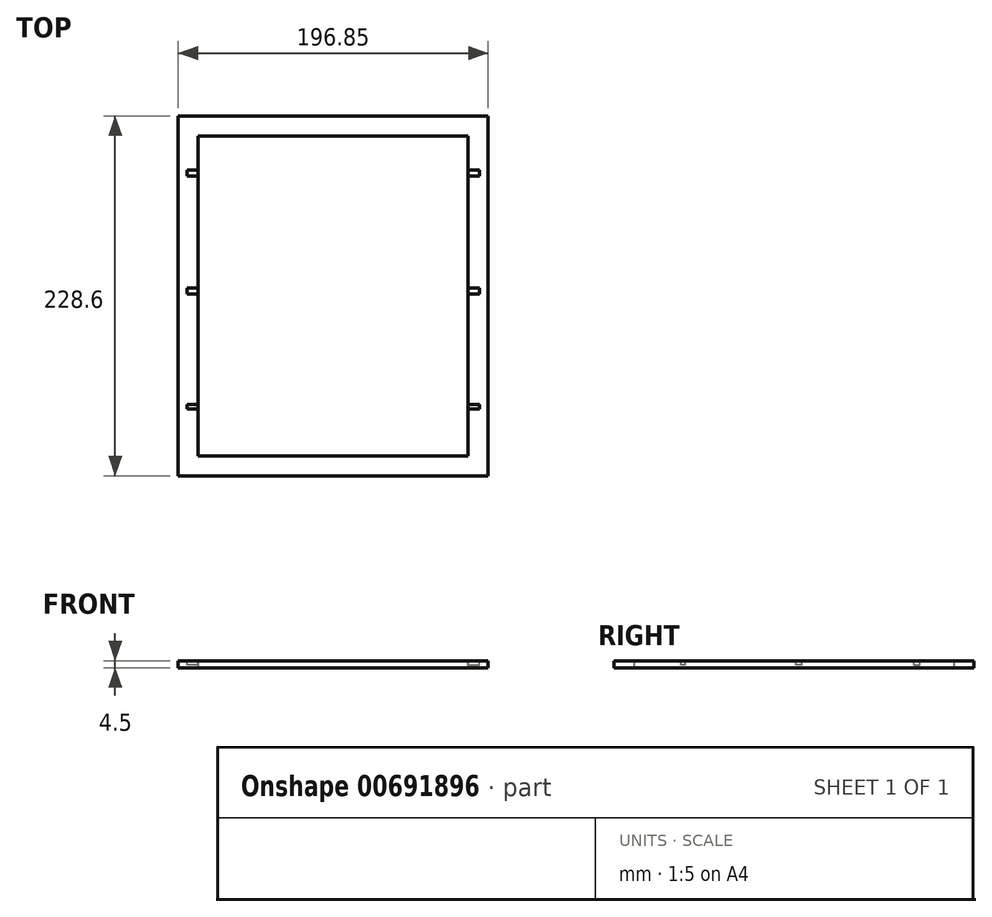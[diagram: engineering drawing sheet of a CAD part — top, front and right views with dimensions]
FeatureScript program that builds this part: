
annotation { "Feature Type Name" : "Feature", "Feature Type Description" : "" }
export const myFeature = defineFeature(function(context is Context, id is Id, definition is map)
    precondition{}
    {
        {
            var Q0;
            Q0=qCreatedBy(makeId("Top.planeOp"),FACE);
            var sketch = newSketch(context, id + "F0", { "sketchPlane" : qUnion([Q0])});
            skLineSegment(sketch, "E0.bottom", {"start": v(-98.45, 125.8) * mm, "end": v(98.4, 125.8) * mm});
            skLineSegment(sketch, "E0.top", {"start": v(-98.45, -102.8) * mm, "end": v(98.4, -102.8) * mm});
            skLineSegment(sketch, "E0.left", {"start": v(-98.45, 125.8) * mm, "end": v(-98.45, -102.8) * mm});
            skLineSegment(sketch, "E0.right", {"start": v(98.4, 125.8) * mm, "end": v(98.4, -102.8) * mm});
            skLineSegment(sketch, "E1.bottom", {"start": v(85.7, -90.1) * mm, "end": v(-85.75, -90.1) * mm});
            skLineSegment(sketch, "E1.top", {"start": v(85.7, 113.1) * mm, "end": v(-85.75, 113.1) * mm});
            skLineSegment(sketch, "E1.left", {"start": v(85.7, -90.1) * mm, "end": v(85.7, 113.1) * mm});
            skLineSegment(sketch, "E1.right", {"start": v(-85.75, -90.1) * mm, "end": v(-85.75, 113.1) * mm});
            skSolve(sketch);
        }
        {
            var Q0;
            Q0=makeQuery(id+"F0.imprint","IMPRINT",FACE,{"disambiguationData":[TD([[makeQuery(id+"F0.imprint","IMPRINT",EDGE,{"derivedFrom":sQuery(id+"F0.wireOp",EDGE,"E1.bottom")}),-1.0]])]});
            var Q1;
            Q1=makeQuery(id+"F0.imprint","IMPRINT",FACE,{"disambiguationData":[TD([[makeQuery(id+"F0.imprint","IMPRINT",EDGE,{"derivedFrom":sQuery(id+"F0.wireOp",EDGE,"E0.bottom")}),-1.0]])]});
            var Q2;
            Q2=sQuery(id+"F0.wireOp",EDGE,"E0.bottom");
            var Q3;
            Q3=sQuery(id+"F0.wireOp",EDGE,"E0.left");
            var Q4;
            Q4=sQuery(id+"F0.wireOp",EDGE,"E0.right");
            var Q5;
            Q5=sQuery(id+"F0.wireOp",EDGE,"E0.top");
            extrude(context, id + "F1", {"entities" : qUnion([Q0, Q1]), "surfaceEntities" : qUnion([Q2, Q3, Q4, Q5]), "depth" : 4.5 * mm, "offsetDistance" : 25.4 * mm});
        }
        {
            var Q0;
            Q0=makeQuery(id+"F0.imprint","IMPRINT",FACE,{"disambiguationData":[TD([[makeQuery(id+"F0.imprint","IMPRINT",EDGE,{"derivedFrom":sQuery(id+"F0.wireOp",EDGE,"E1.bottom")}),-1.0]])]});
            extrude(context, id + "F2", {"entities" : qUnion([Q0]), "operationType" : NewBodyOperationType.REMOVE, "depth" : 4.5 * mm, "offsetDistance" : 25.4 * mm});
        }
        {
            var Q0;
            Q0=makeQuery(id+"F1.opExtrude","CAP_FACE",FACE,{"disambiguationData":[OSD([sQuery(id+"F0.wireOp",EDGE,"E0.bottom"),sQuery(id+"F0.wireOp",EDGE,"E0.top"),sQuery(id+"F0.wireOp",EDGE,"E0.left"),sQuery(id+"F0.wireOp",EDGE,"E0.right")])],"isStart":false});
            var sketch = newSketch(context, id + "F3", { "sketchPlane" : qUnion([Q0])});
            skLineSegment(sketch, "E2.bottom", {"start": v(-85.75, 87.76) * mm, "end": v(-92.86, 87.76) * mm});
            skLineSegment(sketch, "E2.top", {"start": v(-85.75, 91.57) * mm, "end": v(-92.86, 91.57) * mm});
            skLineSegment(sketch, "E2.left", {"start": v(-85.75, 87.76) * mm, "end": v(-85.75, 91.57) * mm});
            skLineSegment(sketch, "E2.right", {"start": v(-92.86, 87.76) * mm, "end": v(-92.86, 91.57) * mm});
            skLineSegment(sketch, "E3.MirrorCS", {"start": v(85.75, 87.76) * mm, "end": v(85.75, 91.57) * mm});
            skLineSegment(sketch, "E4.MirrorCS", {"start": v(85.75, 91.57) * mm, "end": v(92.86, 91.57) * mm});
            skLineSegment(sketch, "E5.MirrorCS", {"start": v(92.86, 87.76) * mm, "end": v(92.86, 91.57) * mm});
            skLineSegment(sketch, "E6.MirrorCS", {"start": v(85.65, 87.76) * mm, "end": v(92.77, 87.76) * mm});
            skLineSegment(sketch, "E7.MirrorCS", {"start": v(92.77, 87.76) * mm, "end": v(92.77, 91.57) * mm});
            skLineSegment(sketch, "E8.MirrorCS", {"start": v(85.65, 87.76) * mm, "end": v(85.65, 91.57) * mm});
            skLineSegment(sketch, "E9.MirrorCS", {"start": v(85.75, 87.76) * mm, "end": v(92.86, 87.76) * mm});
            skLineSegment(sketch, "E10.MirrorCS", {"start": v(85.65, 91.57) * mm, "end": v(92.77, 91.57) * mm});
            skSolve(sketch);
        }
        {
            var Q0;
            {var subQ2=sQuery(id+"F3.wireOp",EDGE,"E2.bottom");Q0=makeQuery(id+"F3.imprint","IMPRINT",FACE,{"disambiguationData":[TD([[makeQuery(id+"F3.imprint","IMPRINT",EDGE,{"derivedFrom":subQ2}),1.0]])]});}
            var sketch = newSketch(context, id + "F4", { "sketchPlane" : qUnion([Q0])});
            skLineSegment(sketch, "E11.bottom", {"start": v(-85.75, -60.46) * mm, "end": v(-92.86, -60.46) * mm});
            skLineSegment(sketch, "E11.top", {"start": v(-85.75, -57.57) * mm, "end": v(-92.86, -57.57) * mm});
            skLineSegment(sketch, "E11.left", {"start": v(-85.75, -60.46) * mm, "end": v(-85.75, -57.57) * mm});
            skLineSegment(sketch, "E11.right", {"start": v(-92.86, -60.46) * mm, "end": v(-92.86, -57.57) * mm});
            skLineSegment(sketch, "E12.MirrorCS", {"start": v(85.7, -57.57) * mm, "end": v(92.8, -57.57) * mm});
            skLineSegment(sketch, "E13.MirrorCS", {"start": v(85.7, -60.46) * mm, "end": v(85.7, -57.57) * mm});
            skLineSegment(sketch, "E14.MirrorCS", {"start": v(85.7, -60.46) * mm, "end": v(92.8, -60.46) * mm});
            skLineSegment(sketch, "E15.MirrorCS", {"start": v(92.8, -60.46) * mm, "end": v(92.8, -57.57) * mm});
            skSolve(sketch);
        }
        {
            var Q0;
            {var subQ0=sQuery(id+"F4.wireOp",EDGE,"E11.right");Q0=makeQuery(id+"F4.imprint","IMPRINT",FACE,{"disambiguationData":[TD([[makeQuery(id+"F4.imprint","IMPRINT",EDGE,{"derivedFrom":subQ0}),-1.0]])]});}
            var Q1;
            Q1=makeQuery(id+"F4.imprint","IMPRINT",FACE,{"disambiguationData":[TD([[makeQuery(id+"F4.imprint","IMPRINT",EDGE,{"derivedFrom":sQuery(id+"F4.wireOp",EDGE,"E12.MirrorCS")}),-1.0]])]});
            extrude(context, id + "F5", {"entities" : qUnion([Q0, Q1]), "operationType" : NewBodyOperationType.REMOVE, "oppositeDirection" : true, "depth" : 2.54 * mm, "offsetDistance" : 25.4 * mm});
        }
        {
            var Q0;
            {var subQ2=sQuery(id+"F3.wireOp",EDGE,"E2.bottom");Q0=makeQuery(id+"F3.imprint","IMPRINT",FACE,{"disambiguationData":[TD([[makeQuery(id+"F3.imprint","IMPRINT",EDGE,{"derivedFrom":subQ2}),1.0]])]});}
            var sketch = newSketch(context, id + "F6", { "sketchPlane" : qUnion([Q0])});
            skLineSegment(sketch, "E16.bottom", {"start": v(85.7, 16.54) * mm, "end": v(92.82, 16.54) * mm});
            skLineSegment(sketch, "E16.top", {"start": v(85.7, 12.73) * mm, "end": v(92.82, 12.73) * mm});
            skLineSegment(sketch, "E16.left", {"start": v(85.7, 16.54) * mm, "end": v(85.7, 12.73) * mm});
            skLineSegment(sketch, "E16.right", {"start": v(92.82, 16.54) * mm, "end": v(92.82, 12.73) * mm});
            skLineSegment(sketch, "E17.MirrorCS", {"start": v(-85.7, 16.54) * mm, "end": v(-92.82, 16.54) * mm});
            skLineSegment(sketch, "E18.MirrorCS", {"start": v(-92.82, 16.54) * mm, "end": v(-92.82, 12.73) * mm});
            skLineSegment(sketch, "E19.MirrorCS", {"start": v(-85.7, 12.73) * mm, "end": v(-92.82, 12.73) * mm});
            skLineSegment(sketch, "E20.MirrorCS", {"start": v(-85.7, 16.54) * mm, "end": v(-85.7, 12.73) * mm});
            skSolve(sketch);
        }
        {
            var Q0;
            Q0=qSketchRegion(id+"F6",true);
            extrude(context, id + "F7", {"entities" : qUnion([Q0]), "operationType" : NewBodyOperationType.REMOVE, "oppositeDirection" : true, "depth" : 2.54 * mm, "offsetDistance" : 25.4 * mm});
        }
        {
            var Q0;
            Q0=qSketchRegion(id+"F3",true);
            extrude(context, id + "F8", {"entities" : qUnion([Q0]), "operationType" : NewBodyOperationType.REMOVE, "oppositeDirection" : true, "depth" : 2.54 * mm, "offsetDistance" : 25.4 * mm});
        }
    });
